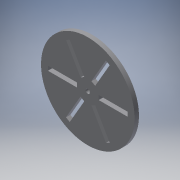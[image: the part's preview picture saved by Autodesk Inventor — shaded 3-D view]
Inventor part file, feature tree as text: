
AUTODESK INVENTOR PART (.ipt)
format: ipt  version: 2019 (Build 230136000, 136)  size: 142,848 bytes
history: native  units: mm
features: other x4, extrude x3, sketch x3, reference x3
ambient origin geometry x8: Origin, YZ Plane, XZ Plane, XY Plane, X Axis, Y Axis, Z Axis, Center Point
bodies: Body1 (feature_tree)
feature tree (13):
  other  "Твердое тело1"
  extrude  "Выдавливание1"  Depth=129.0mm
  extrude  "Выдавливание2"  Depth=6.0mm TaperAngle=0.0deg
  extrude  "Выдавливание3"  Depth=2.5mm
  sketch  "Эскиз1"
  reference  "Ссылка1"
  sketch  "Эскиз2"
  reference  "Ссылка2"
  sketch  "Эскиз3"
  reference  "Ссылка3"
  parser-record x1  (decoder bookkeeping rows leaked as tree rows — omitted from the tree; the rows remain in map.json)
  other  "kowsh.iam"
  other  "Двигатель:1"
note: 1 file-system path scrubbed to <path> (originals preserved in map.json)
